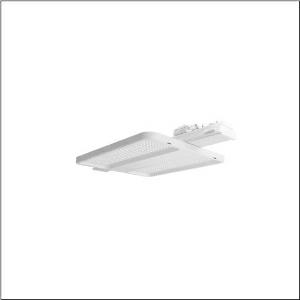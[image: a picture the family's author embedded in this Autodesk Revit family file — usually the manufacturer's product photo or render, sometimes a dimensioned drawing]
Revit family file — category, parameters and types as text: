
# Revit family: highbay_11_fur_licross_r__tragschiene_midi_51hn12da4kla_79e9
name_source: partatom
category: Lighting Fixtures
units: mm (PartAtom-declared; Revit-internal decimal feet)

## family parameters
Cut with Voids When Loaded = No
Host = Face
Light Source = No
Part Type = Normal
Room Calculation Point = No
Round Connector Dimension = Use Diameter
Shared = No

## types (1)
- --- (1 x LED, 23000 lm, 117.3 W, 4000K)
    Apparent Load = 117 VA
    CIE Flux Codes = 87 98 100 100 100
    Color Rendering = 80
    Color Temperature = 4000K
    Default Elevation = 1800 mm
    Description = high bay luminaire Highbay 11 for Licross® trunking rail midi; direct symmetric wide distribution, light control with lens of PMMA; UGR ≤ 22 (X = 4H | Y = 8H | S = 0.25H | reflection values 70/50/20); luminous flux: 23.000lm; light colour: 840, colour temperature: 4000K, MacAdam ≤ 2 SDCM (initial), colour rendering: CRI > 80; luminous efficacy: 196,1lm/W; rated service life: 100.000h (L95/B50) at AT= 25°C; control: DALI 2; luminaire connection: plug, 5-pole, with phase selectionmains connection: 230..240V, AC 50/60Hz; connected load: 117,3W; protection rating (complete): IP64; insulation class (complete): insulation class I (protective earthing); protection symbol: D; impact resistance: IK07; certification: CE, ENEC, VDE, UKCA; internal wiring halogen-free; luminaire LABS conformity tested according to VDMA 24364:2018-05; corresponds to IFS (International Featured Standards) requirements for safety and quality in the food industry; housing frame of high-performance plastic PA6, matt traffic white (RAL 9016); cover of PMMA; fixing on rail side of steel, galvanised, white; blank cover of PC/ABS, traffic white (RAL 9016); dimension (LxWxH): 750 x 442 x 71mm; permissible operating ambient temperature: -40..+55°C (reducing of maximum allowable ambient temperature of 5°C with ceiling mounting); packaging unit: 1 piece
    Height = 72 mm  [stored 0.23622 ft]
    Lamp = 1 x LED
    Lamp Light Flux = 23000 lm
    Lamp Power = 117.3 W
    Lamp count = 1
    Length = 474 mm
    Luminous efficacy = 196 lm/W
    Manufacturer = Siteco
    ModVariant = No
    Model = 51HN12DA4KLA
    Mounting Place = Ceiling
    Mounting Type = Pendant
    Number of Poles = 1
    OnlyDefault = Yes
    Power Factor = 1
    Product Name = Highbay 11 für Licross® Tragschiene midi
    Product group = high bay luminaire
    ProductGroupID = 901
    Protection Class = Protection class I
    Protection Degree = IP 64
    RLX_Detail_Level = 1
    RLX_Emergency_Light_Flux = 0 lm
    RLX_Emergency_Type = 0
    RLX_Emergency_Type_DB = No
    RlxData = <blob elided: 17081 chars, md5=a35ffb8b>
    Socket = socket
    Standby Power = 0 W
    System Light Flux = 23000 lm
    System Power = 117 W
    Type Comments = factory setting: luminous flux: 100 % | dim-lin: 254 | 534 mA
    Type Image = l_1363258.jpg
    URL = http://relux.com
    VarID = @adj_014709
    Voltage = 0 V
    Weight = 0.00 kg
    Width = 442 mm

note: [stored X ft] marks values corroborated as IEEE doubles in the binary element streams (Revit-internal decimal feet)

## geometry (parser evidence)
native form markers: Blend x4, Sweep x11
no freeform markers — native parametric forms only
